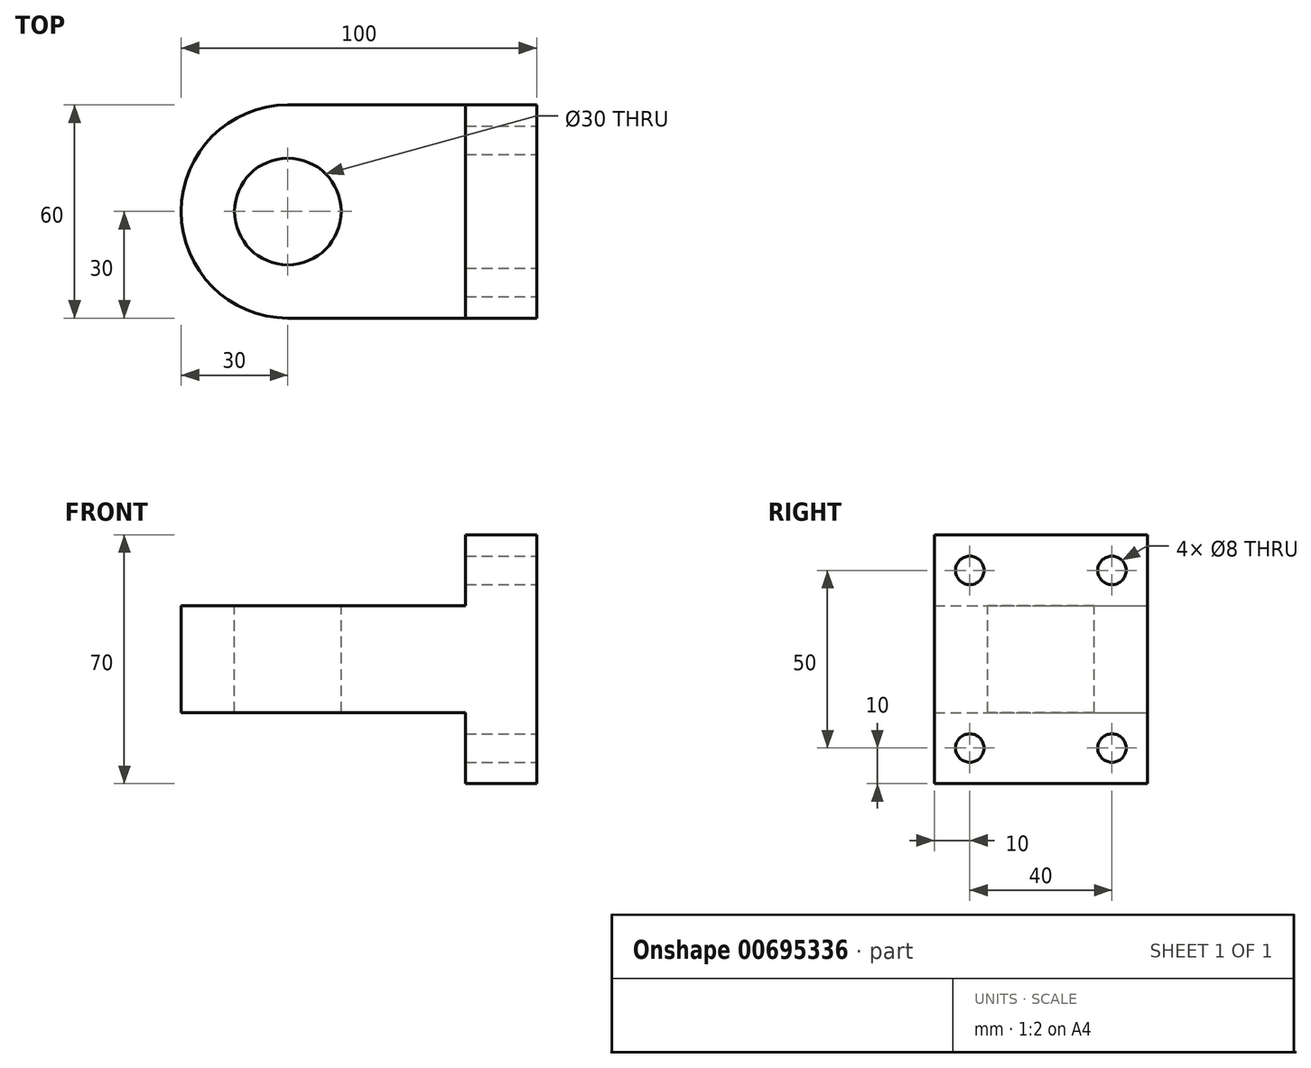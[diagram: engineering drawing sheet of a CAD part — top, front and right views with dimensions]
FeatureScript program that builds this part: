
annotation { "Feature Type Name" : "Feature", "Feature Type Description" : "" }
export const myFeature = defineFeature(function(context is Context, id is Id, definition is map)
    precondition{}
    {
        {
            var Q0;
            Q0=qCreatedBy(makeId("Front.planeOp"),FACE);
            var sketch = newSketch(context, id + "F0", { "sketchPlane" : qUnion([Q0])});
            skLineSegment(sketch, "E0", {"start": v(0, 0) * mm, "end": v(0, 35) * mm});
            skLineSegment(sketch, "E1", {"start": v(0, 35) * mm, "end": v(-20, 35) * mm});
            skLineSegment(sketch, "E2", {"start": v(-20, 35) * mm, "end": v(-20, 15) * mm});
            skLineSegment(sketch, "E3", {"start": v(-20, 15) * mm, "end": v(-100, 15) * mm});
            skLineSegment(sketch, "E4", {"start": v(-100, 15) * mm, "end": v(-100, 0) * mm});
            skLineSegment(sketch, "E5", {"start": v(-100, 0) * mm, "end": v(0, 0) * mm});
            skSolve(sketch);
        }
        {
            var Q0;
            Q0 = qSketchRegion(id + "F0", true);
            extrude(context, id + "F1", {"entities" : qUnion([Q0]), "endBound" : BoundingType.SYMMETRIC, "depth" : 60 * mm, "offsetDistance" : 25 * mm});
        }
        {
            var Q0;
            Q0=makeQuery(id+"F1.opExtrude","CAP_EDGE",EDGE,{"disambiguationData":[OSD([sQuery(id+"F0.wireOp",EDGE,"E4")])],"isStart":false});
            fillet(context, id + "F2", {"entities" : qUnion([Q0]), "radius" : 30 * mm, "tangentPropagation" : true, "allowEdgeOverflow" : false});
        }
        {
            var Q0;
            Q0=makeQuery(id+"F1.opExtrude","CAP_EDGE",EDGE,{"disambiguationData":[OSD([sQuery(id+"F0.wireOp",EDGE,"E4")])],"isStart":true});
            fillet(context, id + "F3", {"entities" : qUnion([Q0]), "radius" : 30 * mm, "tangentPropagation" : true, "allowEdgeOverflow" : false});
        }
        {
            var Q0;
            Q0=makeQuery(id+"F1.opExtrude","SWEPT_FACE",FACE,{"disambiguationData":[OSD([sQuery(id+"F0.wireOp",EDGE,"E3")])]});
            var sketch = newSketch(context, id + "F4", { "sketchPlane" : qUnion([Q0])});
            skCircle(sketch, "E6", {"center": v(-70, 0) * mm, "radius": 15 * mm});
            skSolve(sketch);
        }
        {
            var Q0;
            Q0 = qSketchRegion(id + "F4", true);
            extrude(context, id + "F5", {"entities" : qUnion([Q0]), "operationType" : NewBodyOperationType.REMOVE, "oppositeDirection" : true, "depth" : 25 * mm, "offsetDistance" : 25 * mm});
        }
        {
            var Q0;
            Q0=makeQuery(id+"F1.opExtrude","SWEPT_BODY",BODY,{"disambiguationData":[OSD([sQuery(id+"F0.wireOp",EDGE,"E0"),sQuery(id+"F0.wireOp",EDGE,"E1"),sQuery(id+"F0.wireOp",EDGE,"E2"),sQuery(id+"F0.wireOp",EDGE,"E3"),sQuery(id+"F0.wireOp",EDGE,"E4"),sQuery(id+"F0.wireOp",EDGE,"E5")])]});
            var Q1;
            Q1=qCreatedBy(makeId("Top.planeOp"),FACE);
            mirror(context, id + "F6", {"operationType" : NewBodyOperationType.ADD, "entities" : qUnion([Q0]), "mirrorPlane" : qUnion([Q1])});
        }
        {
            var Q0;
            {var subQ0=makeQuery(id+"F1.opExtrude","SWEPT_FACE",FACE,{"disambiguationData":[OSD([sQuery(id+"F0.wireOp",EDGE,"E0")])]});Q0=makeQuery(id+"F6.boolean.opBoolean","MERGE",FACE,{"derivedFrom":[subQ0,makeQuery(id+"F6.opPattern","COPY",FACE,{"derivedFrom":subQ0,"instanceName":"1"})]});}
            var sketch = newSketch(context, id + "F7", { "sketchPlane" : qUnion([Q0])});
            skLineSegment(sketch, "E7", {"start": v(-30, -35) * mm, "end": v(-30, -25) * mm});
            skLineSegment(sketch, "E8", {"start": v(-30, -25) * mm, "end": v(-20, -25) * mm});
            skCircle(sketch, "E9", {"center": v(-20, -25) * mm, "radius": 4 * mm});
            skCircle(sketch, "E10.0.1.0", {"center": v(-20, 25) * mm, "radius": 4 * mm});
            skCircle(sketch, "E10.1.0.0", {"center": v(20, -25) * mm, "radius": 4 * mm});
            skCircle(sketch, "E10.1.1.0", {"center": v(20, 25) * mm, "radius": 4 * mm});
            skLineSegment(sketch, "E10.direction1", {"start": v(-20, -25) * mm, "end": v(20, -25) * mm, "construction": true});
            skLineSegment(sketch, "E10.direction2", {"start": v(-20, -25) * mm, "end": v(-20, 25) * mm, "construction": true});
            skSolve(sketch);
        }
        {
            var Q0;
            Q0 = qSketchRegion(id + "F7", true);
            extrude(context, id + "F8", {"entities" : qUnion([Q0]), "operationType" : NewBodyOperationType.REMOVE, "endBound" : BoundingType.UP_TO_NEXT, "oppositeDirection" : true, "depth" : 25 * mm, "offsetDistance" : 25 * mm});
        }
    });
